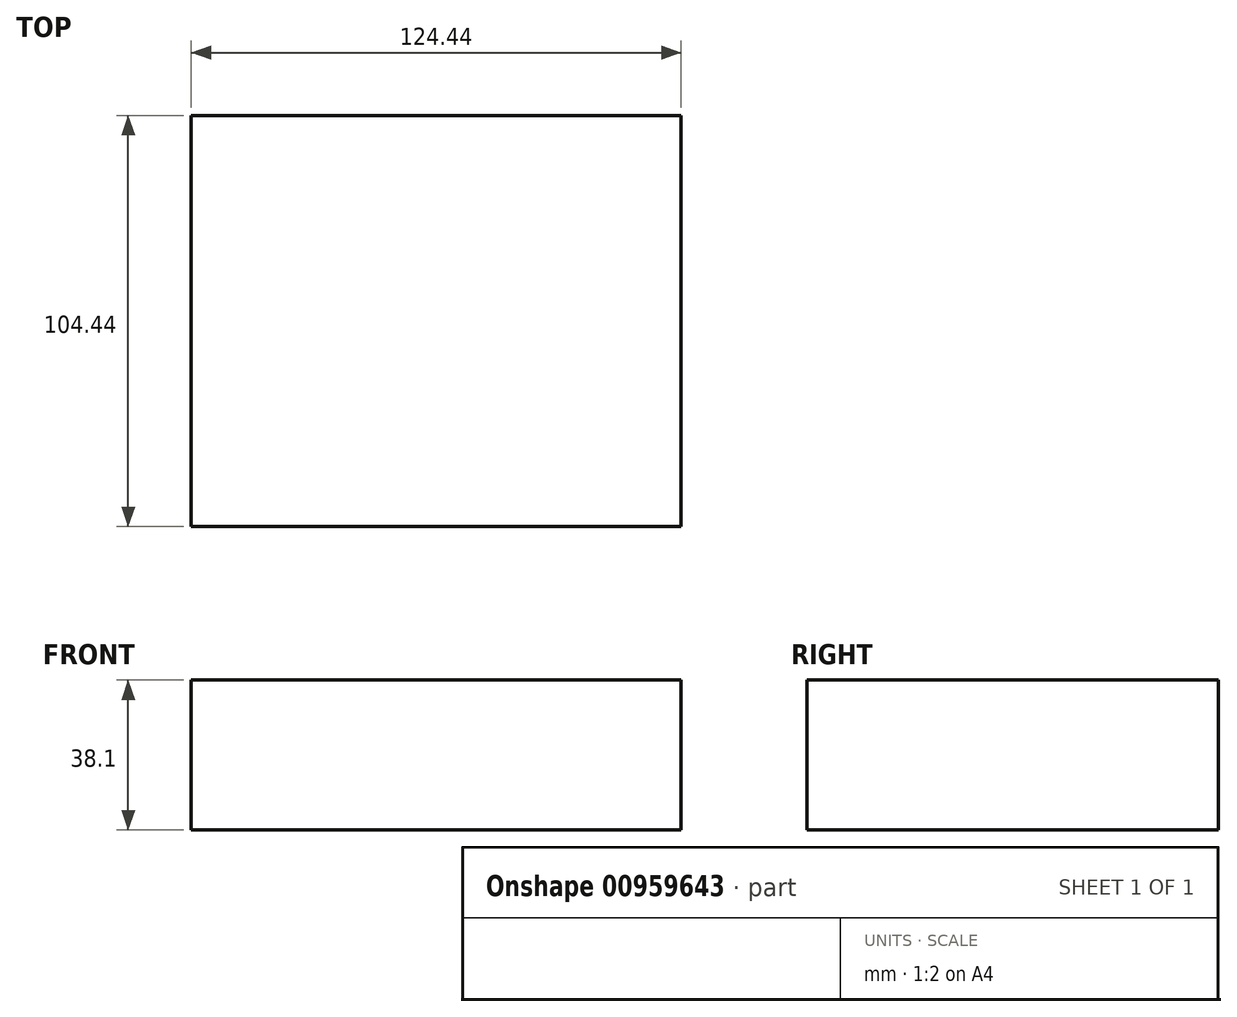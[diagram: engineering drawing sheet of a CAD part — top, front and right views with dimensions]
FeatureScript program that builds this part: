
annotation { "Feature Type Name" : "Feature", "Feature Type Description" : "" }
export const myFeature = defineFeature(function(context is Context, id is Id, definition is map)
    precondition{}
    {
        {
            var Q0;
            Q0=qCreatedBy(makeId("Top.planeOp"),FACE);
            var sketch = newSketch(context, id + "F0", { "sketchPlane" : qUnion([Q0])});
            skLineSegment(sketch, "E0.bottom", {"start": v(-62.22, 53.76) * mm, "end": v(62.22, 53.76) * mm});
            skLineSegment(sketch, "E0.top", {"start": v(-62.22, -50.68) * mm, "end": v(62.22, -50.68) * mm});
            skLineSegment(sketch, "E0.left", {"start": v(-62.22, 53.76) * mm, "end": v(-62.22, -50.68) * mm});
            skLineSegment(sketch, "E0.right", {"start": v(62.22, 53.76) * mm, "end": v(62.22, -50.68) * mm});
            skSolve(sketch);
        }
        {
            var Q0;
            Q0=makeQuery(id+"F0.imprint","IMPRINT",FACE,{"disambiguationData":[TD([[makeQuery(id+"F0.imprint","IMPRINT",EDGE,{"derivedFrom":sQuery(id+"F0.wireOp",EDGE,"E0.bottom")}),-1.0]])]});
            extrude(context, id + "F1", {"entities" : qUnion([Q0]), "depth" : 38.1 * mm, "offsetDistance" : 25.4 * mm});
        }
    });
